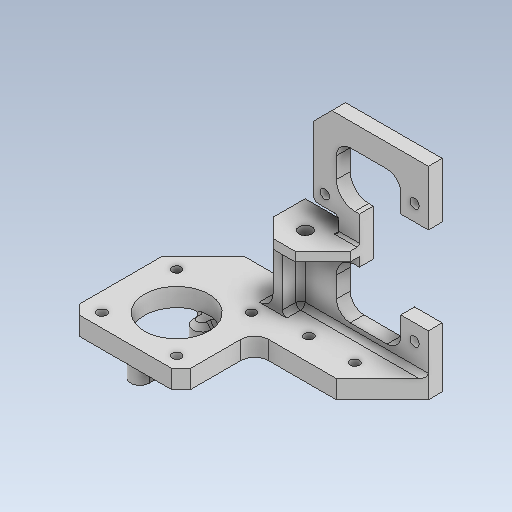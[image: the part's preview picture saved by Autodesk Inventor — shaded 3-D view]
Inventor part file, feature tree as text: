
AUTODESK INVENTOR PART (.ipt)
format: ipt  version: 2020 (Build 240168000, 168)  size: 598,528 bytes
history: native  units: mm
features: extrude x17, sketch x17, projected_geometry x17, fillet x12, reference x11, thicken_offset x10, other x8, chamfer x7
ambient origin geometry x8: Origin, YZ Plane, XZ Plane, XY Plane, X Axis, Y Axis, Z Axis, Center Point
bodies: Solid1 (feature_tree)
feature tree (99):
  extrude  "Extrusion1"  Depth=15.0mm
  extrude  "Extrusion2"  Depth=2.0mm
  extrude  "Extrusion3"  Depth=8.0mm
  extrude  "Extrusion4"  Depth=1.0mm
  extrude  "Extrusion5"  Depth=2.0mm
  extrude  "Extrusion6"  Depth=5.0mm
  fillet  "Fillet1"  Radius=3.85mm
  thicken_offset  "Thicken1"
  extrude  "Extrusion7"  Depth=8.0mm
  fillet  "Fillet3"  Radius=8.0mm
  extrude  "Extrusion8"  Depth=10.0mm TaperAngle=0.0deg
  thicken_offset  "Thicken2"
  thicken_offset  "Thicken3"
  extrude  "Extrusion9"  Depth=3.85mm
  extrude  "Extrusion10"  Depth=10.0mm TaperAngle=0.0deg
  extrude  "Extrusion11"  Depth=4.0mm
  extrude  "Extrusion12"  Depth=5.0mm
  chamfer  "Chamfer1"  Distance=5.0mm
  thicken_offset  "Thicken4"
  chamfer  "Chamfer2"  Distance=9.0mm
  extrude  "Extrusion13"  Depth=25.0mm
  thicken_offset  "Thicken5"
  thicken_offset  "Thicken6"
  extrude  "Extrusion14"  Depth=5.0mm
  thicken_offset  "Thicken7"
  thicken_offset  "Thicken8"
  fillet  "Fillet4"  Radius=6.0mm
  fillet  "Fillet5"  Radius=7.0mm
  extrude  "Extrusion15"  Depth=3.0mm TaperAngle=0.0deg
  chamfer  "Chamfer3"  Distance=3.0mm
  extrude  "Extrusion16"  Depth=4.0mm
  extrude  "Extrusion17"  Depth=50.0mm
  fillet  "Fillet6"  Radius=3.0mm
  fillet  "Fillet7"  Radius=30.0mm
  fillet  "Fillet8"  Radius=3.0mm
  chamfer  "Chamfer4"  Distance=3.0mm
  fillet  "Fillet9"  Radius=1.0mm
  fillet  "Fillet10"  Radius=1.0mm
  chamfer  "Chamfer5"  Distance=30.0mm
  fillet  "Fillet11"  Radius=16.0mm
  thicken_offset  "Thicken9"
  thicken_offset  "Thicken10"
  fillet  "Fillet12"  Radius=12.0mm
  chamfer  "Chamfer6"  Distance=14.0mm
  chamfer  "Chamfer7"  Distance=30.0mm
  fillet  "Fillet13"  Radius=2.0mm
  sketch  "Sketch1"  dims[d0=5.0mm d1=15.0mm]
  reference  "Reference1"
  reference  "Reference2"
  sketch  "Sketch2"  dims[d2=3.0mm d3=0.0mm d4=2.0mm]
  projected_geometry  "Projected Loop1"
  sketch  "Sketch3"  dims[d5=6.0mm d6=8.0mm]
  projected_geometry  "Projected Loop2"
  sketch  "Sketch4"  dims[d7=3.0mm d8=0.0mm d9=1.0mm]
  reference  "Reference3"
  projected_geometry  "Projected Loop3"
  projected_geometry  "Projected Loop4"
  projected_geometry  "Projected Loop5"
  sketch  "Sketch5"  dims[d10=10.0mm d11=2.0mm]
  reference  "Reference4"
  sketch  "Sketch6"  dims[d12=10.0mm d13=0.0mm d14=5.0mm d15=3.85mm]
  projected_geometry  "Projected Loop6"
  projected_geometry  "Projected Loop7"
  sketch  "Sketch7"  dims[d16=3.0mm d17=8.0mm d18=8.0mm]
  reference  "Reference5"
  reference  "Reference6"
  sketch  "Sketch8"  dims[d19=11.9mm d20=10.0mm d21=0.0mm]
  projected_geometry  "Projected Loop8"
  sketch  "Sketch9"  dims[d22=5.0mm d23=3.85mm]
  projected_geometry  "Projected Loop9"
  sketch  "Sketch10"  dims[d24=2.8mm d25=10.0mm d26=0.0mm]
  projected_geometry  "Projected Loop10"
  reference  "Reference7"
  sketch  "Sketch11"  dims[d27=2.5mm d28=0.0mm d29=4.0mm]
  projected_geometry  "Projected Loop11"
  sketch  "Sketch12"  dims[d31=1.1mm d32=1.0mm d33=5.0mm]
  projected_geometry  "Projected Loop12"
  sketch  "Sketch13"  dims[d34=9.0mm]
  reference  "Reference8"
  reference  "Reference9"
  reference  "Reference10"
  reference  "Reference11"
  sketch  "Sketch14"  dims[d35=25.0mm]
  projected_geometry  "Projected Loop13"
  sketch  "Sketch15"  dims[d36=5.0mm]
  projected_geometry  "Projected Loop14"
  sketch  "Sketch16"  dims[d37=6.0mm]
  projected_geometry  "Projected Loop15"
  projected_geometry  "Projected Loop16"
  sketch  "Sketch17"  dims[d38=7.0mm d39=5.0mm d40=9.0mm d41=25.0mm d42=5.0mm d43=6.0mm d44=7.0mm d45=3.0mm d46=0.0mm d47=3.0mm d48=4.0mm d49=50.0mm d50=3.0mm d51=30.0mm d52=0.0mm d53=3.0mm d54=3.0mm d55=1.0mm d56=1.0mm d57=30.0mm d58=0.0mm d59=16.0mm d60=12.0mm d61=14.0mm d62=30.0mm d63=0.0mm d64=2.0mm d65=17.5mm d66=30.0mm d67=0.0mm d68=30.0mm d69=0.0mm d70=10.0mm d71=2.0mm d72=45.0deg d73=4.0mm d74=4.0mm d75=7.0mm d76=2.0mm d77=45.0deg d78=30.0mm d79=0.0mm d80=2.0mm d81=2.0mm d82=2.0mm d83=2.0mm d84=30.0mm d85=0.0mm d86=1.0mm d87=1.0mm d88=0.5mm d89=0.5mm d90=0.5mm d91=1.0mm d92=5.5mm d93=5.5mm d94=2.5mm d95=4.0mm d96=2.5mm d97=4.0mm d98=4.3mm d99=0.0mm d100=1.0mm d101=2.0mm d102=45.0deg d103=1.8mm d104=1.8mm d105=4.0mm d106=0.0mm d107=6.0mm d108=10.0mm d109=2.0mm d110=2.0mm d111=4.0mm d112=0.0mm d113=1.0mm d114=1.0mm d115=3.0mm d116=6.0mm d117=2.0mm d118=45.0deg d119=0.5mm d120=2.0mm d121=2.0mm d122=2.0mm d123=45.0deg d124=3.0mm d125=1.0mm d126=1.0mm d127=1.0mm d128=1.0mm d129=1.0mm d130=4.0mm d131=2.0mm d132=45.0deg d133=4.0mm d134=2.0mm d135=45.0deg d136=0.5mm]
  projected_geometry  "Projected Loop17"
  parser-record x1  (decoder bookkeeping rows leaked as tree rows — omitted from the tree; the rows remain in map.json)
  other  "tip_3_n_base_ass.iam"
  other  "ext_pin_shell_2:1"
  other  "bl_tube_ass_2:1"
  other  "bl_tube_hn_1:1"
  other  "bearing_3_6_2:5"
  other  "mot_27_ass:2"
  other  "mot_27_2:1"
note: 1 file-system path scrubbed to <path> (originals preserved in map.json)
